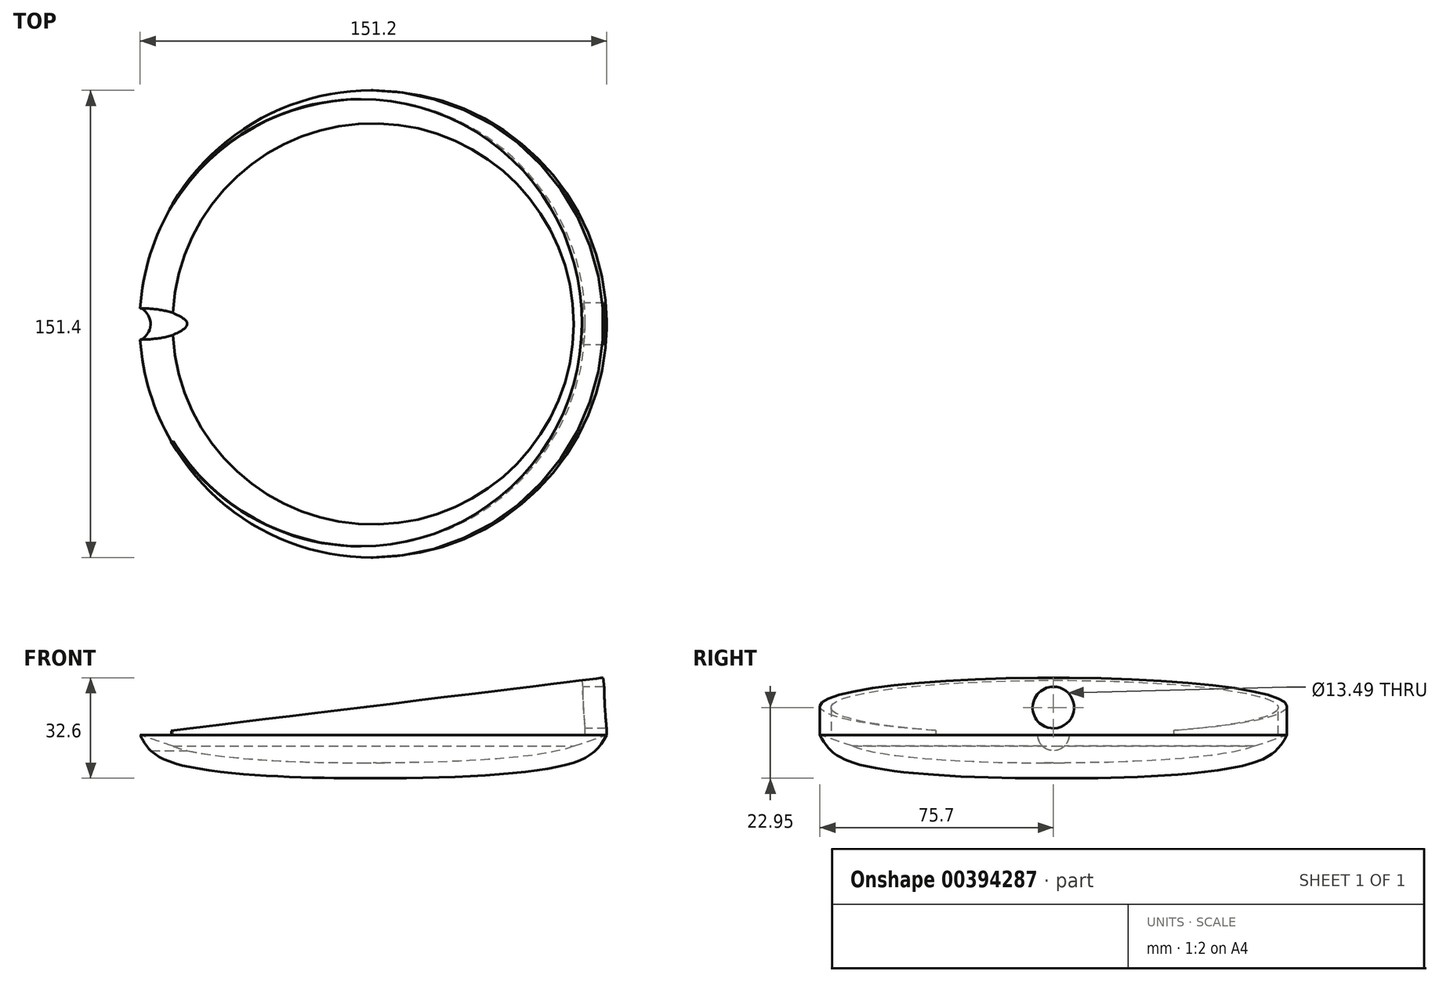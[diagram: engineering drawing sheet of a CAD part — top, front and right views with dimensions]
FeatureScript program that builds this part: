
annotation { "Feature Type Name" : "Feature", "Feature Type Description" : "" }
export const myFeature = defineFeature(function(context is Context, id is Id, definition is map)
    precondition{}
    {
        {
            var Q0;
            Q0=qCreatedBy(makeId("Front.planeOp"),FACE);
            var sketch = newSketch(context, id + "F0", { "sketchPlane" : qUnion([Q0])});
            skFitSpline(sketch, "E0", {"points": [v(75.67, -0.03) * mm, v(58.75, -10.56) * mm, v(-57.5, -10.38) * mm, v(-76.5, 0) * mm], "startDerivative": vector(-35.3, -73.77) * mm, "endDerivative": vector(-39.7, 72) * mm});
            skFitSpline(sketch, "E1.0", {"points": [v(71.1, 2.16) * mm, v(70.8, 1.54) * mm, v(70.2, 0.46) * mm, v(69.29, -0.77) * mm, v(68.23, -1.78) * mm, v(66.83, -2.74) * mm, v(64.85, -3.69) * mm, v(62.15, -4.6) * mm, v(59.23, -5.3) * mm, v(56.46, -5.83) * mm, v(53.4, -6.34) * mm, v(49.1, -6.91) * mm, v(43.27, -7.5) * mm, v(36.88, -8) * mm, v(27.76, -8.52) * mm, v(15.44, -8.93) * mm, v(-0.06, -9.04) * mm, v(-15.56, -8.76) * mm, v(-27.87, -8.23) * mm, v(-37, -7.62) * mm, v(-43.38, -7.09) * mm, v(-49.2, -6.47) * mm, v(-53.52, -5.89) * mm, v(-56.58, -5.4) * mm, v(-59.37, -4.87) * mm, v(-62.34, -4.19) * mm, v(-65.16, -3.3) * mm, v(-67.29, -2.37) * mm, v(-68.86, -1.4) * mm, v(-70.05, -0.38) * mm, v(-71.07, 0.83) * mm, v(-71.73, 1.86) * mm, v(-72.05, 2.45) * mm]});
            skLineSegment(sketch, "E2", {"start": v(0, -14.05) * mm, "end": v(0, -8.97) * mm});
            skLineSegment(sketch, "E3", {"start": v(0, -8.97) * mm, "end": v(0, -14.05) * mm});
            skLineSegment(sketch, "E4", {"start": v(75.67, -0.03) * mm, "end": v(63.8, -4.03) * mm});
            skSolve(sketch);
        }
        {
            var Q0;
            Q0=makeQuery(id+"F0.imprint","IMPRINT",FACE,{"disambiguationData":[TD([[makeQuery(id+"F0.imprint","IMPRINT",EDGE,{"derivedFrom":sQuery(id+"F0.wireOp",EDGE,"E0")}),-1.0]])]});
            var Q1;
            Q1=sQuery(id+"F0.wireOp",EDGE,"E3");
            revolve(context, id + "F1", {"entities" : qUnion([Q0]), "axis" : qUnion([Q1]), "revolveType" : RevolveType.FULL});
        }
        {
            var Q0;
            Q0=qCreatedBy(makeId("Right.planeOp"),FACE);
            var sketch = newSketch(context, id + "F2", { "sketchPlane" : qUnion([Q0])});
            skCircle(sketch, "E5", {"center": v(0, 0) * mm, "radius": 5.08 * mm});
            skSolve(sketch);
        }
        {
            var Q0;
            Q0 = qSketchRegion(id + "F2", true);
            extrude(context, id + "F3", {"entities" : qUnion([Q0]), "operationType" : NewBodyOperationType.REMOVE, "oppositeDirection" : true, "depth" : 101.6 * mm});
        }
        {
            var Q0;
            Q0=qCreatedBy(makeId("Top.planeOp"),FACE);
            var sketch = newSketch(context, id + "F4", { "sketchPlane" : qUnion([Q0])});
            skArc(sketch, "E6", {"start": v(0, -75.7) * mm, "mid": v(75.7, 0) * mm, "end": v(0, 75.7) * mm});
            skLineSegment(sketch, "E7", {"start": v(-76.44, 0) * mm, "end": v(-76.44, -31.39) * mm});
            skArc(sketch, "E8", {"start": v(-65.38, -38.16) * mm, "mid": v(75.7, -0.44) * mm, "end": v(-64.92, 38.93) * mm});
            skArc(sketch, "E9", {"start": v(68.76, 0) * mm, "mid": v(16.76, 69.98) * mm, "end": v(-64.72, 38.93) * mm});
            skArc(sketch, "E10", {"start": v(-64.72, -38.16) * mm, "mid": v(16.39, -69.32) * mm, "end": v(68.76, 0) * mm});
            skLineSegment(sketch, "E11", {"start": v(-64.72, -38.16) * mm, "end": v(-65.38, -38.16) * mm});
            skLineSegment(sketch, "E12", {"start": v(-64.72, 38.93) * mm, "end": v(-64.92, 38.93) * mm});
            skPoint(sketch, "E13.orphan", {"position": v(-75.7, 0) * mm});
            skSolve(sketch);
        }
        {
            var Q0;
            Q0 = qSketchRegion(id + "F4", true);
            var Q1;
            Q1=sQuery(id+"F4.wireOp",EDGE,"E7");
            revolve(context, id + "F5", {"operationType" : NewBodyOperationType.ADD, "entities" : qUnion([Q0]), "axis" : qUnion([Q1]), "revolveType" : RevolveType.ONE_DIRECTION, "angle" : 7 * degree});
        }
        {
            var Q0;
            Q0=qCreatedBy(makeId("Right.planeOp"),FACE);
            var sketch = newSketch(context, id + "F6", { "sketchPlane" : qUnion([Q0])});
            skCircle(sketch, "E14", {"center": v(0, 8.9) * mm, "radius": 6.74 * mm});
            skSolve(sketch);
        }
        {
            var Q0;
            Q0 = qSketchRegion(id + "F6", true);
            extrude(context, id + "F7", {"entities" : qUnion([Q0]), "operationType" : NewBodyOperationType.REMOVE, "depth" : 101.6 * mm});
        }
    });
